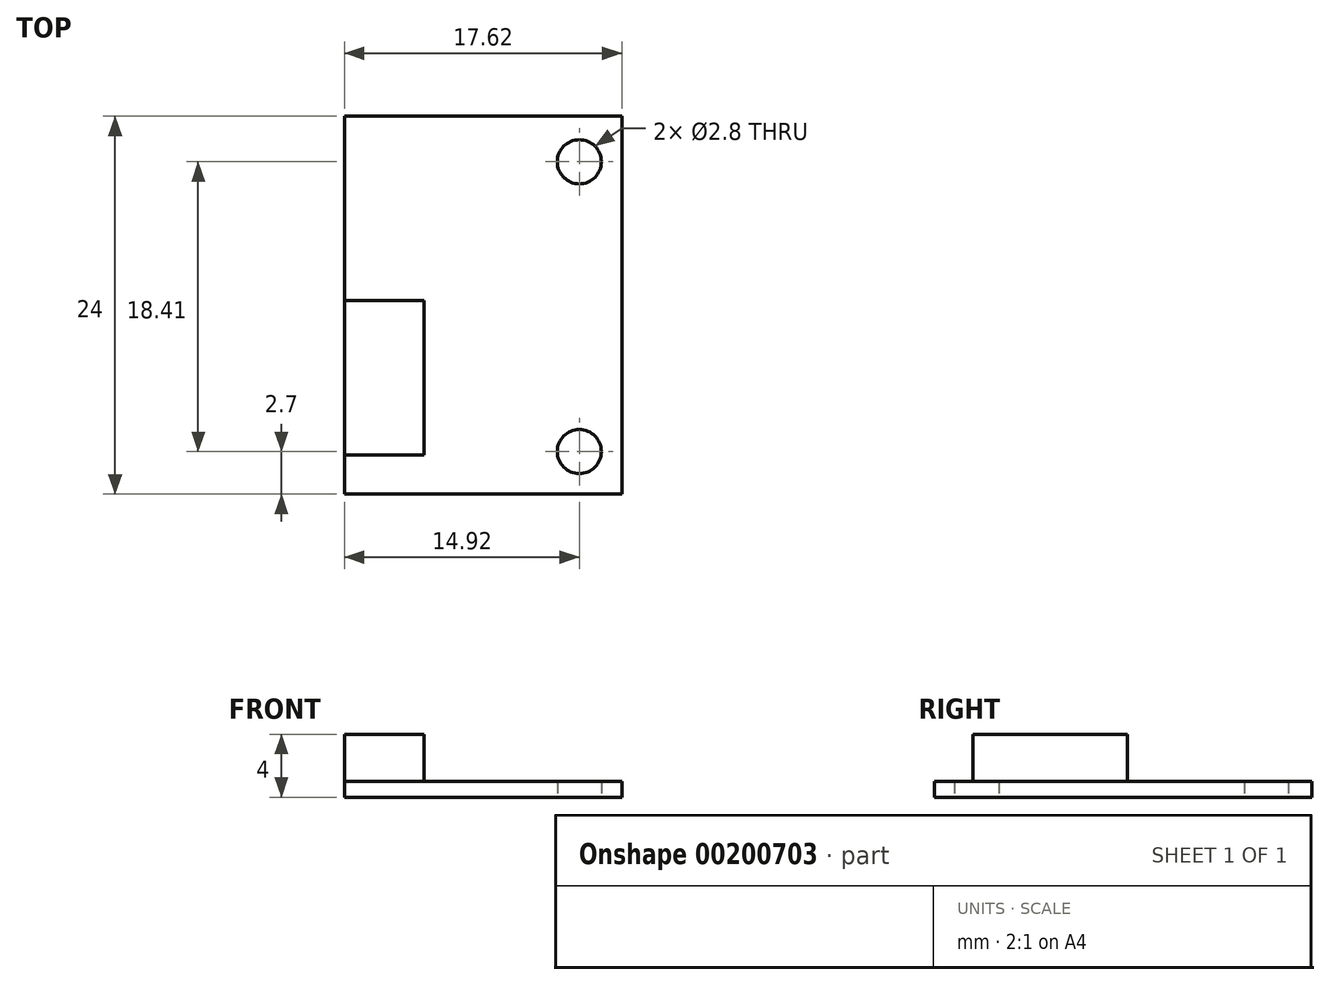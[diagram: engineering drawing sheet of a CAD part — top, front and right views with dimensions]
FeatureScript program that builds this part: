
annotation { "Feature Type Name" : "Feature", "Feature Type Description" : "" }
export const myFeature = defineFeature(function(context is Context, id is Id, definition is map)
    precondition{}
    {
        {
            var Q0;
            Q0=qCreatedBy(makeId("Top.planeOp"),FACE);
            var sketch = newSketch(context, id + "F0", { "sketchPlane" : qUnion([Q0])});
            skLineSegment(sketch, "E0.bottom", {"start": v(0, 0) * mm, "end": v(17.62, 0) * mm});
            skLineSegment(sketch, "E0.top", {"start": v(0, 24) * mm, "end": v(17.62, 24) * mm});
            skLineSegment(sketch, "E0.left", {"start": v(0, 0) * mm, "end": v(0, 24) * mm});
            skLineSegment(sketch, "E0.right", {"start": v(17.62, 0) * mm, "end": v(17.62, 24) * mm});
            skSolve(sketch);
        }
        {
            var Q0;
            Q0=makeQuery(id+"F0.imprint","IMPRINT",FACE,{"disambiguationData":[TD([[makeQuery(id+"F0.imprint","IMPRINT",EDGE,{"derivedFrom":sQuery(id+"F0.wireOp",EDGE,"E0.bottom")}),1.0]])]});
            var sketch = newSketch(context, id + "F1", { "sketchPlane" : qUnion([Q0])});
            skCircle(sketch, "E1", {"center": v(14.92, 2.7) * mm, "radius": 1.4 * mm});
            skCircle(sketch, "E2", {"center": v(14.92, 21.1) * mm, "radius": 1.4 * mm});
            skSolve(sketch);
        }
        {
            var Q0;
            Q0 = qSketchRegion(id + "F0", true);
            extrude(context, id + "F2", {"entities" : qUnion([Q0]), "depth" : 1 * mm});
        }
        {
            var Q0;
            Q0 = qSketchRegion(id + "F1", true);
            extrude(context, id + "F3", {"entities" : qUnion([Q0]), "operationType" : NewBodyOperationType.REMOVE, "depth" : 3 * mm});
        }
        {
            var Q0;
            Q0=makeQuery(id+"F2.opExtrude","CAP_FACE",FACE,{"disambiguationData":[OSD([sQuery(id+"F0.wireOp",EDGE,"E0.bottom"),sQuery(id+"F0.wireOp",EDGE,"E0.top"),sQuery(id+"F0.wireOp",EDGE,"E0.left"),sQuery(id+"F0.wireOp",EDGE,"E0.right")])],"isStart":false});
            var sketch = newSketch(context, id + "F4", { "sketchPlane" : qUnion([Q0])});
            skLineSegment(sketch, "E3.bottom", {"start": v(0, 2.48) * mm, "end": v(5.07, 2.48) * mm});
            skLineSegment(sketch, "E3.top", {"start": v(0, 12.28) * mm, "end": v(5.07, 12.28) * mm});
            skLineSegment(sketch, "E3.left", {"start": v(0, 2.48) * mm, "end": v(0, 12.28) * mm});
            skLineSegment(sketch, "E3.right", {"start": v(5.07, 2.48) * mm, "end": v(5.07, 12.28) * mm});
            skSolve(sketch);
        }
        {
            var Q0;
            Q0=makeQuery(id+"F4.imprint","IMPRINT",FACE,{"disambiguationData":[TD([[makeQuery(id+"F4.imprint","IMPRINT",EDGE,{"derivedFrom":sQuery(id+"F4.wireOp",EDGE,"E3.bottom")}),1.0]])]});
            extrude(context, id + "F5", {"entities" : qUnion([Q0]), "operationType" : NewBodyOperationType.ADD, "depth" : 3 * mm});
        }
    });
